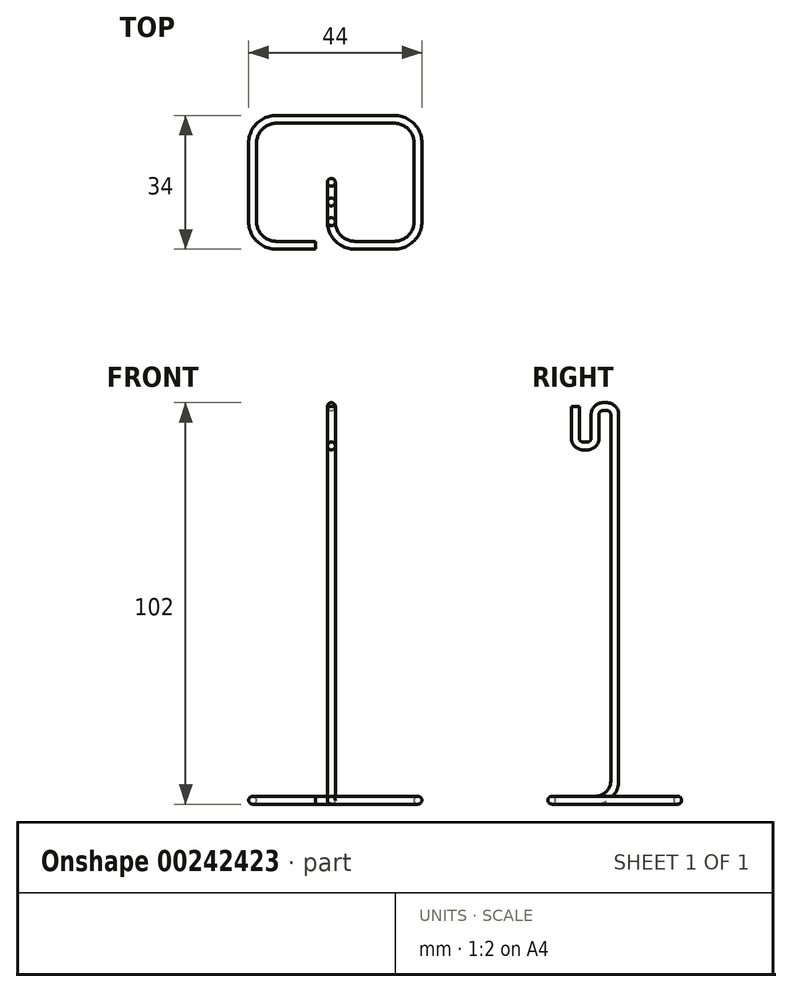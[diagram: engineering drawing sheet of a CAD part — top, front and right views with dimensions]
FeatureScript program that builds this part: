
annotation { "Feature Type Name" : "Feature", "Feature Type Description" : "" }
export const myFeature = defineFeature(function(context is Context, id is Id, definition is map)
    precondition{}
    {
        {
            var Q0;
            Q0=qCreatedBy(makeId("Right.planeOp"),FACE);
            var sketch = newSketch(context, id + "F0", { "sketchPlane" : qUnion([Q0])});
            skLineSegment(sketch, "E0", {"start": v(-37.42, 100) * mm, "end": v(-37.42, 92) * mm});
            skLineSegment(sketch, "E1", {"start": v(-35.42, 90) * mm, "end": v(-34.42, 90) * mm});
            skLineSegment(sketch, "E2", {"start": v(-32.42, 92) * mm, "end": v(-32.42, 98) * mm});
            skLineSegment(sketch, "E3", {"start": v(-30.42, 100) * mm, "end": v(-29.42, 100) * mm});
            skLineSegment(sketch, "E4", {"start": v(-27.42, 98) * mm, "end": v(-27.42, 5) * mm});
            skLineSegment(sketch, "E5", {"start": v(-32.42, 0) * mm, "end": v(-37.42, 0) * mm});
            skPoint(sketch, "E6.visualSharp", {"position": v(-37.42, 90) * mm});
            skArc(sketch, "E6.filletArc", {"start": v(-37.42, 92) * mm, "mid": v(-36.84, 90.59) * mm, "end": v(-35.42, 90) * mm});
            skPoint(sketch, "E7.visualSharp", {"position": v(-32.42, 90) * mm});
            skArc(sketch, "E7.filletArc", {"start": v(-34.42, 90) * mm, "mid": v(-33.01, 90.59) * mm, "end": v(-32.42, 92) * mm});
            skPoint(sketch, "E8.visualSharp", {"position": v(-32.42, 100) * mm});
            skArc(sketch, "E8.filletArc", {"start": v(-30.42, 100) * mm, "mid": v(-31.84, 99.41) * mm, "end": v(-32.42, 98) * mm});
            skPoint(sketch, "E9.visualSharp", {"position": v(-27.42, 100) * mm});
            skArc(sketch, "E9.filletArc", {"start": v(-27.42, 98) * mm, "mid": v(-28.01, 99.41) * mm, "end": v(-29.42, 100) * mm});
            skPoint(sketch, "E10.visualSharp", {"position": v(-27.42, 0) * mm});
            skArc(sketch, "E10.filletArc", {"start": v(-32.42, 0) * mm, "mid": v(-28.89, 1.46) * mm, "end": v(-27.42, 5) * mm});
            skSolve(sketch);
        }
        {
            var Q0;
            Q0=qCreatedBy(makeId("Top.planeOp"),FACE);
            var sketch = newSketch(context, id + "F1", { "sketchPlane" : qUnion([Q0])});
            skPoint(sketch, "E11.0", {"position": v(0, -37.42) * mm});
            skLineSegment(sketch, "E12", {"start": v(0, -37.42) * mm, "end": v(0, -37.42) * mm});
            skLineSegment(sketch, "E13", {"start": v(5, -42.42) * mm, "end": v(15, -42.42) * mm});
            skLineSegment(sketch, "E14", {"start": v(20, -37.42) * mm, "end": v(20, -17.42) * mm});
            skLineSegment(sketch, "E15", {"start": v(15, -12.42) * mm, "end": v(-15, -12.42) * mm});
            skLineSegment(sketch, "E16", {"start": v(-20, -17.42) * mm, "end": v(-20, -37.42) * mm});
            skLineSegment(sketch, "E17", {"start": v(-15, -42.42) * mm, "end": v(-5, -42.42) * mm});
            skPoint(sketch, "E18.visualSharp", {"position": v(0, -42.42) * mm});
            skArc(sketch, "E18.filletArc", {"start": v(0, -37.42) * mm, "mid": v(1.46, -40.96) * mm, "end": v(5, -42.42) * mm});
            skPoint(sketch, "E19.visualSharp", {"position": v(20, -42.42) * mm});
            skArc(sketch, "E19.filletArc", {"start": v(15, -42.42) * mm, "mid": v(18.54, -40.96) * mm, "end": v(20, -37.42) * mm});
            skPoint(sketch, "E20.visualSharp", {"position": v(20, -12.42) * mm});
            skArc(sketch, "E20.filletArc", {"start": v(20, -17.42) * mm, "mid": v(18.54, -13.89) * mm, "end": v(15, -12.42) * mm});
            skPoint(sketch, "E21.visualSharp", {"position": v(-20, -12.42) * mm});
            skArc(sketch, "E21.filletArc", {"start": v(-15, -12.42) * mm, "mid": v(-18.54, -13.89) * mm, "end": v(-20, -17.42) * mm});
            skPoint(sketch, "E22.visualSharp", {"position": v(-20, -42.42) * mm});
            skArc(sketch, "E22.filletArc", {"start": v(-20, -37.42) * mm, "mid": v(-18.54, -40.96) * mm, "end": v(-15, -42.42) * mm});
            skSolve(sketch);
        }
        {
            var Q0;
            Q0=sQuery(id+"F1.wireOp",VERTEX,"E17.end");
            var Q1;
            Q1=qCreatedBy(makeId("Right.planeOp"),FACE);
            cPlane(context, id + "F2", {"entities" : qUnion([Q0, Q1]), "cplaneType" : CPlaneType.PLANE_POINT, "offset" : 25 * mm, "width" : 150 * mm, "height" : 150 * mm});
        }
        {
            var Q0;
            Q0=qCreatedBy(id+"F2.planeOp",FACE);
            var sketch = newSketch(context, id + "F3", { "sketchPlane" : qUnion([Q0])});
            skPoint(sketch, "E23.0", {"position": v(-42.42, 0) * mm});
            skCircle(sketch, "E24", {"center": v(-43.42, 0) * mm, "radius": 1 * mm});
            skSolve(sketch);
        }
        {
            var Q0;
            Q0=makeQuery(id+"F3.imprint","IMPRINT",FACE,{"disambiguationData":[TD([[makeQuery(id+"F3.imprint","IMPRINT",EDGE,{"derivedFrom":sQuery(id+"F3.wireOp",EDGE,"E24")}),1.0]])]});
            var Q1;
            Q1=sQuery(id+"F1.wireOp",EDGE,"E17");
            var Q2;
            Q2=sQuery(id+"F1.wireOp",EDGE,"E22.filletArc");
            var Q3;
            Q3=sQuery(id+"F1.wireOp",EDGE,"E16");
            var Q4;
            Q4=sQuery(id+"F1.wireOp",EDGE,"E21.filletArc");
            var Q5;
            Q5=sQuery(id+"F1.wireOp",EDGE,"E15");
            var Q6;
            Q6=sQuery(id+"F1.wireOp",EDGE,"E20.filletArc");
            var Q7;
            Q7=sQuery(id+"F1.wireOp",EDGE,"E14");
            var Q8;
            Q8=sQuery(id+"F1.wireOp",EDGE,"E19.filletArc");
            var Q9;
            Q9=sQuery(id+"F1.wireOp",EDGE,"E13");
            var Q10;
            Q10=sQuery(id+"F1.wireOp",EDGE,"E18.filletArc");
            var Q11;
            Q11=sQuery(id+"F0.wireOp",EDGE,"E5");
            var Q12;
            Q12=sQuery(id+"F0.wireOp",EDGE,"E10.filletArc");
            var Q13;
            Q13=sQuery(id+"F0.wireOp",EDGE,"E4");
            var Q14;
            Q14=sQuery(id+"F0.wireOp",EDGE,"E9.filletArc");
            var Q15;
            Q15=sQuery(id+"F0.wireOp",EDGE,"E3");
            var Q16;
            Q16=sQuery(id+"F0.wireOp",EDGE,"E8.filletArc");
            var Q17;
            Q17=sQuery(id+"F0.wireOp",EDGE,"E2");
            var Q18;
            Q18=sQuery(id+"F0.wireOp",EDGE,"E7.filletArc");
            var Q19;
            Q19=sQuery(id+"F0.wireOp",EDGE,"E1");
            var Q20;
            Q20=sQuery(id+"F0.wireOp",EDGE,"E6.filletArc");
            var Q21;
            Q21=sQuery(id+"F0.wireOp",EDGE,"E0");
            sweep(context, id + "F4", {"profiles" : qUnion([Q0]), "path" : qUnion([Q1, Q2, Q3, Q4, Q5, Q6, Q7, Q8, Q9, Q10, Q11, Q12, Q13, Q14, Q15, Q16, Q17, Q18, Q19, Q20, Q21])});
        }
    });
